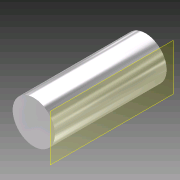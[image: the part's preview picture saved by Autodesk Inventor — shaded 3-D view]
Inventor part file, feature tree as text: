
AUTODESK INVENTOR PART (.ipt)
format: ipt  version: 2011 (Build 150239000, 239)  size: 71,680 bytes
history: native  units: in
note: dims shown in document units (in); Inventor stores cm internally (conversion verified against a paired STEP export)
features: sketch x2, extrude x1, plane x1
ambient origin geometry x8: Origin, YZ Plane, XZ Plane, XY Plane, X Axis, Y Axis, Z Axis, Center Point
bodies: Solid1 (feature_tree)
feature tree (4):
  extrude  "Extrusion1"  Depth=5.502in TaperAngle=0.0deg
  plane  "Work Plane1"
  sketch  "Sketch2"  dims[d3=1.5in]
  sketch  "Sketch1"  dims[d0=2.08in d1=5.502in d2=0.0in]
